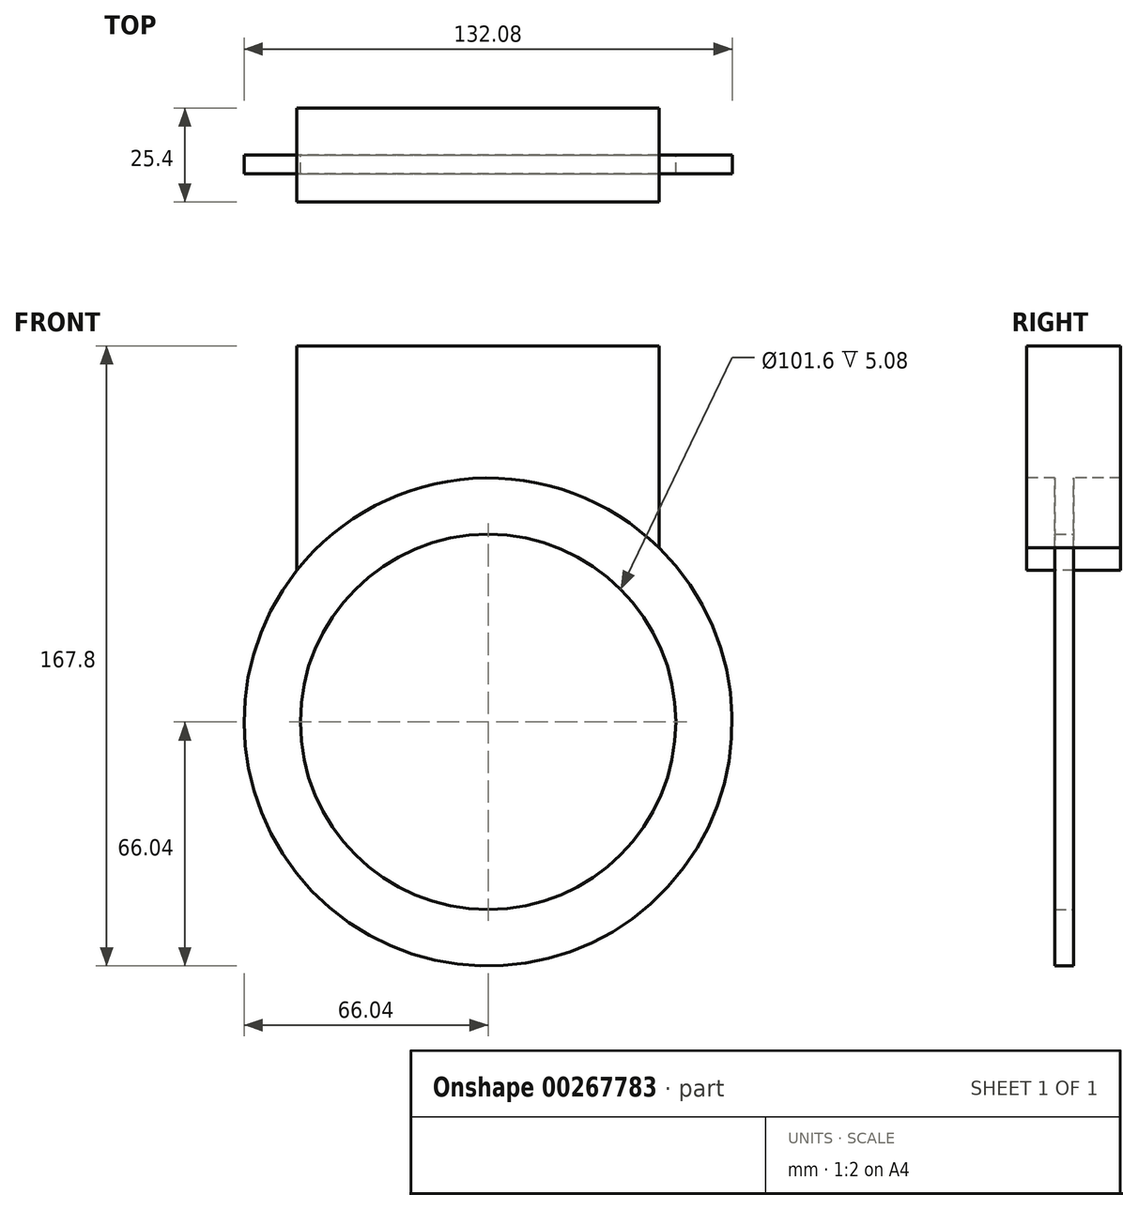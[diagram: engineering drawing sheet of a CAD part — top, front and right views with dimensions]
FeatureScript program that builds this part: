
annotation { "Feature Type Name" : "Feature", "Feature Type Description" : "" }
export const myFeature = defineFeature(function(context is Context, id is Id, definition is map)
    precondition{}
    {
        {
            var Q0;
            Q0=qCreatedBy(makeId("Front.planeOp"),FACE);
            var sketch = newSketch(context, id + "F0", { "sketchPlane" : qUnion([Q0])});
            skCircle(sketch, "E0", {"center": v(0, 0) * mm, "radius": 66.04 * mm});
            skCircle(sketch, "E1.0", {"center": v(0, 0) * mm, "radius": 50.8 * mm});
            skLineSegment(sketch, "E2.bottom", {"start": v(-51.75, 101.76) * mm, "end": v(46.25, 101.76) * mm});
            skLineSegment(sketch, "E2.top", {"start": v(-51.75, 25.56) * mm, "end": v(46.25, 25.56) * mm});
            skLineSegment(sketch, "E2.left", {"start": v(-51.75, 101.76) * mm, "end": v(-51.75, 25.56) * mm});
            skLineSegment(sketch, "E2.right", {"start": v(46.25, 101.76) * mm, "end": v(46.25, 25.56) * mm});
            skSolve(sketch);
        }
        {
            var Q0;
            Q0=makeQuery(id+"F0.imprint","IMPRINT",FACE,{"disambiguationData":[TD([[makeQuery(id+"F0.imprint","IMPRINT",EDGE,{"derivedFrom":sQuery(id+"F0.wireOp",EDGE,"E0")}),1.0]])]});
            extrude(context, id + "F1", {"entities" : qUnion([Q0]), "depth" : 5.08 * mm});
        }
        {
            var Q0;
            {var subQ5=sQuery(id+"F0.wireOp",EDGE,"E2.bottom");Q0=makeQuery(id+"F0.imprint","IMPRINT",FACE,{"disambiguationData":[TD([[makeQuery(id+"F0.imprint","IMPRINT",EDGE,{"derivedFrom":subQ5}),-1.0]])]});}
            extrude(context, id + "F2", {"entities" : qUnion([Q0]), "operationType" : NewBodyOperationType.ADD, "endBound" : BoundingType.SYMMETRIC, "oppositeDirection" : true, "depth" : 25.4 * mm});
        }
    });
